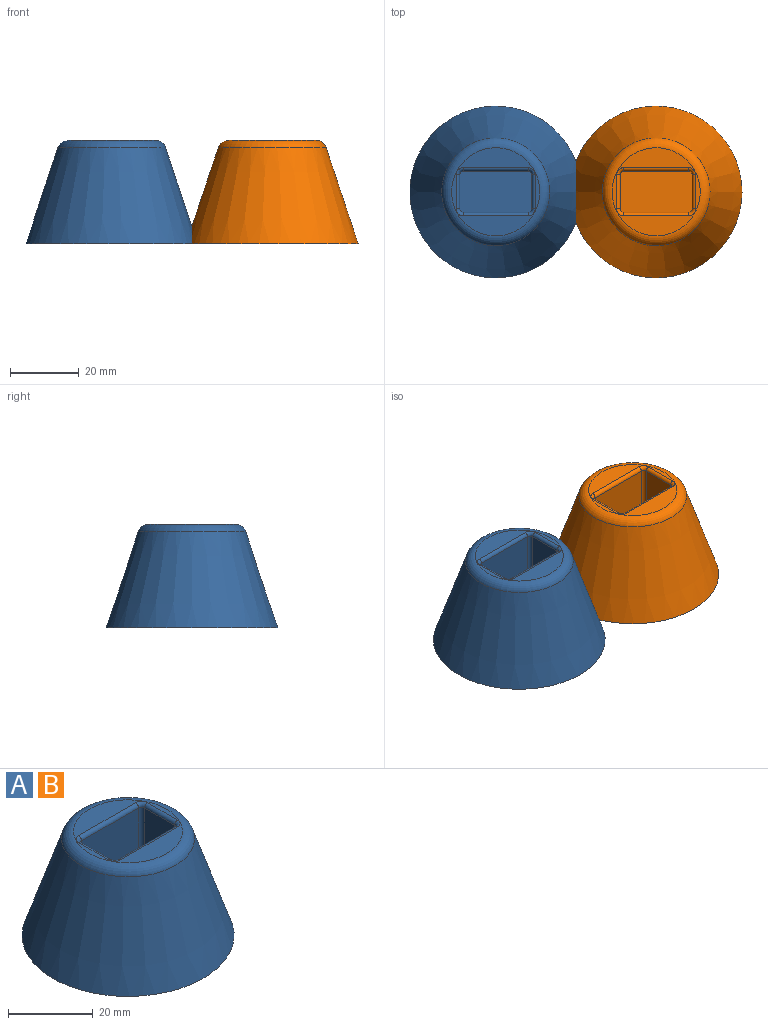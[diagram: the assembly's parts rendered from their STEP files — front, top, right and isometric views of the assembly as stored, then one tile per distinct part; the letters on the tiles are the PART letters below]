
ASSEMBLY  parts=2 mates=1
PART A: 42 faces, bbox 50x50x30 mm
  f0: plane 11.37x1.5mm, normal (0,-1,0), area 16.7mm2, adj f4,f6,f8,f35
  f1: plane 11.37x1.5mm, normal (0,1,0), area 16.7mm2, adj f4,f6,f8,f35
  f2: plane 15.87x1.5mm, normal (-1,0,0), area 23.4mm2, adj f4,f8,f20,f41
  f3: plane 15.87x1.5mm, normal (1,0,0), area 23.4mm2, adj f4,f8,f20,f41
  f4: cone r=23.58mm half-angle=18.4deg, axis (0,0,-1), area 3504.1mm2, adj f0,f1,f2,f3,f5,f6,f8,f15
  f5: plane 28.51x15.01mm, normal (-1,0,0), area 422.7mm2, adj f4,f8,f17,f19,f20,f34,f36,f37
  f6: plane 28.51x15.01mm, normal (1,0,0), area 422.7mm2, adj f0,f1,f4,f8,f15,f19,f20,f35
  f7: plane 25.68x25.68mm, normal (0,0,1), area 199.2mm2, adj f23,f24,f25,f26,f29,f30,f31,f32
  f8: plane 50x50mm, normal (0,0,-1), area 764.3mm2, adj f0,f1,f2,f3,f4,f5,f6,f9
  f9: cone r=25mm half-angle=18.4deg, axis (0,0,-1), area 3765.4mm2, adj f8,f33
  f10: plane 27x19mm, normal (0,-1,0), area 513mm2, adj f14,f21,f26,f27
  f11: plane 27x10mm, normal (1,0,0), area 270mm2, adj f14,f27,f28,f32
  f12: plane 27x19mm, normal (0,1,0), area 513mm2, adj f14,f22,f28,f29
  f13: plane 27x10mm, normal (-1,0,0), area 270mm2, adj f14,f21,f22,f23
  f14: plane 21x12mm, normal (0,0,1), area 251.1mm2, adj f10,f11,f12,f13,f21,f22,f27,f28
  f15: plane 14.1x1.92mm, normal (0,0,-1), area 18.3mm2, adj f4,f6
  f16: plane 23.45x6.42mm, normal (0,0,-1), area 106.1mm2, adj f4,f19
  f17: plane 14.1x1.92mm, normal (0,0,-1), area 18.3mm2, adj f4,f5
  f18: plane 23.45x6.42mm, normal (0,0,-1), area 106.1mm2, adj f4,f20
  f19: plane 28.5x24mm, normal (0,1,0), area 679.3mm2, adj f4,f5,f6,f8,f16,f38,f39,f40
  f20: plane 28.5x24mm, normal (0,-1,0), area 679.3mm2, adj f2,f3,f4,f5,f6,f8,f18,f41
  f21: cylinder r=1mm len=27mm, axis (0,0,-1), area 42.4mm2, adj f10,f13,f14,f24
  f22: cylinder r=1mm len=27mm, axis (0,0,1), area 42.4mm2, adj f12,f13,f14,f25
  f23: cylinder r=1mm len=10mm, axis (0,-1,0), area 15.7mm2, adj f7,f13,f24,f25
  f24: torus R=2mm, axis (0,0,1), area 3.4mm2, adj f7,f21,f23,f26
  f25: torus R=2mm, axis (0,0,1), area 3.4mm2, adj f7,f22,f23,f29
  f26: cylinder r=1mm len=19mm, axis (1,0,0), area 29.8mm2, adj f7,f10,f24,f30
  f27: cylinder r=1mm len=27mm, axis (0,0,1), area 42.4mm2, adj f10,f11,f14,f30
  f28: cylinder r=1mm len=27mm, axis (0,0,-1), area 42.4mm2, adj f11,f12,f14,f31
  f29: cylinder r=1mm len=19mm, axis (-1,0,0), area 29.8mm2, adj f7,f12,f25,f31
  f30: torus R=2mm, axis (0,0,1), area 3.4mm2, adj f7,f26,f27,f32
  f31: torus R=2mm, axis (0,0,1), area 3.4mm2, adj f7,f28,f29,f32
  f32: cylinder r=1mm len=10mm, axis (0,1,0), area 15.7mm2, adj f7,f11,f30,f31
  f33: torus R=12.84mm, axis (0,0,1), area 340.9mm2, adj f7,f9
  f34: plane 10.92x3mm, normal (0,0,1), area 32.7mm2, adj f4,f5,f36,f37
  f35: plane 10.92x3mm, normal (0,0,1), area 32.7mm2, adj f0,f1,f4,f6
  f36: plane 11.37x1.5mm, normal (0,-1,0), area 16.7mm2, adj f4,f5,f8,f34
  f37: plane 11.37x1.5mm, normal (0,1,0), area 16.7mm2, adj f4,f5,f8,f34
  f38: plane 15.87x1.5mm, normal (1,0,0), area 23.4mm2, adj f4,f8,f19,f40
  f39: plane 15.87x1.5mm, normal (-1,0,0), area 23.4mm2, adj f4,f8,f19,f40
  f40: plane 15.42x3mm, normal (0,0,1), area 46.2mm2, adj f4,f19,f38,f39
  f41: plane 15.42x3mm, normal (0,0,1), area 46.2mm2, adj f2,f3,f4,f20
PART B: same geometry as A
PLACE A t=(-4.8,6.86,5.46)mm
PLACE B t=(41.94,6.86,5.46)mm
MATE planar A.f8 <-> B.f8  axis (0,0,-1) through (18.57,8.36,5.46)mm
